# Revit family: Unonovesette_TRAIL 54 Q
name_source: partatom
category: Lighting Fixtures
units: mm (PartAtom-declared; Revit-internal decimal feet)

## family parameters
Cut with Voids When Loaded = No
Host = Face
Light Source = No
Part Type = Normal
Room Calculation Point = No
Round Connector Dimension = Use Diameter
Shared = No

## types (1)
- Unonovesette_TRAIL 54 Q
    197_Accessories = ACC.050 - Fixing springs
    197_Beam_Angle = Asymmetric
    197_Colour = 197_Black_Anodized
    197_Colour_Rendering_Index_CRI = >90
    197_Colour_Temperature = 2700 K
    197_Degree_of_Protection = IP68
    197_Dimension = L54xW54xH56
    197_Housing_Box = 197_Black
    197_Insulation_Class = III
    197_Lamp = LED
    197_Luminous_Flux = 17 lm
    197_Model = Trail 54 Q
    197_Photometrics = 197_TRAIL 54 Q - Photometrics : TR5Q.27.A.XX.02
    197_Product_Code = TR5Q.27.A.05.02
    197_Rated_Voltage = 230 V
    197_Wattage = 2 W
    197_Weight = 0.21 kg
    Apparent Load = 2 VA
    Default Elevation = 1219 mm
    IfcExportAs = IfcLightFixtureType
    IfcExportType = DIRECTIONSOURCE
    Manufacturer = unonovesette ltd
    Model = Trail 54 Q
    URL = https://unonovesette.it
    Uniclass2015Code = Pr_70_70_48_71
    Uniclass2015Title = Recessed luminaires
    Uniclass2015Version = Product v1.12

## geometry (parser evidence)
native form markers: Blend x2, Sweep x5
no freeform markers — native parametric forms only
